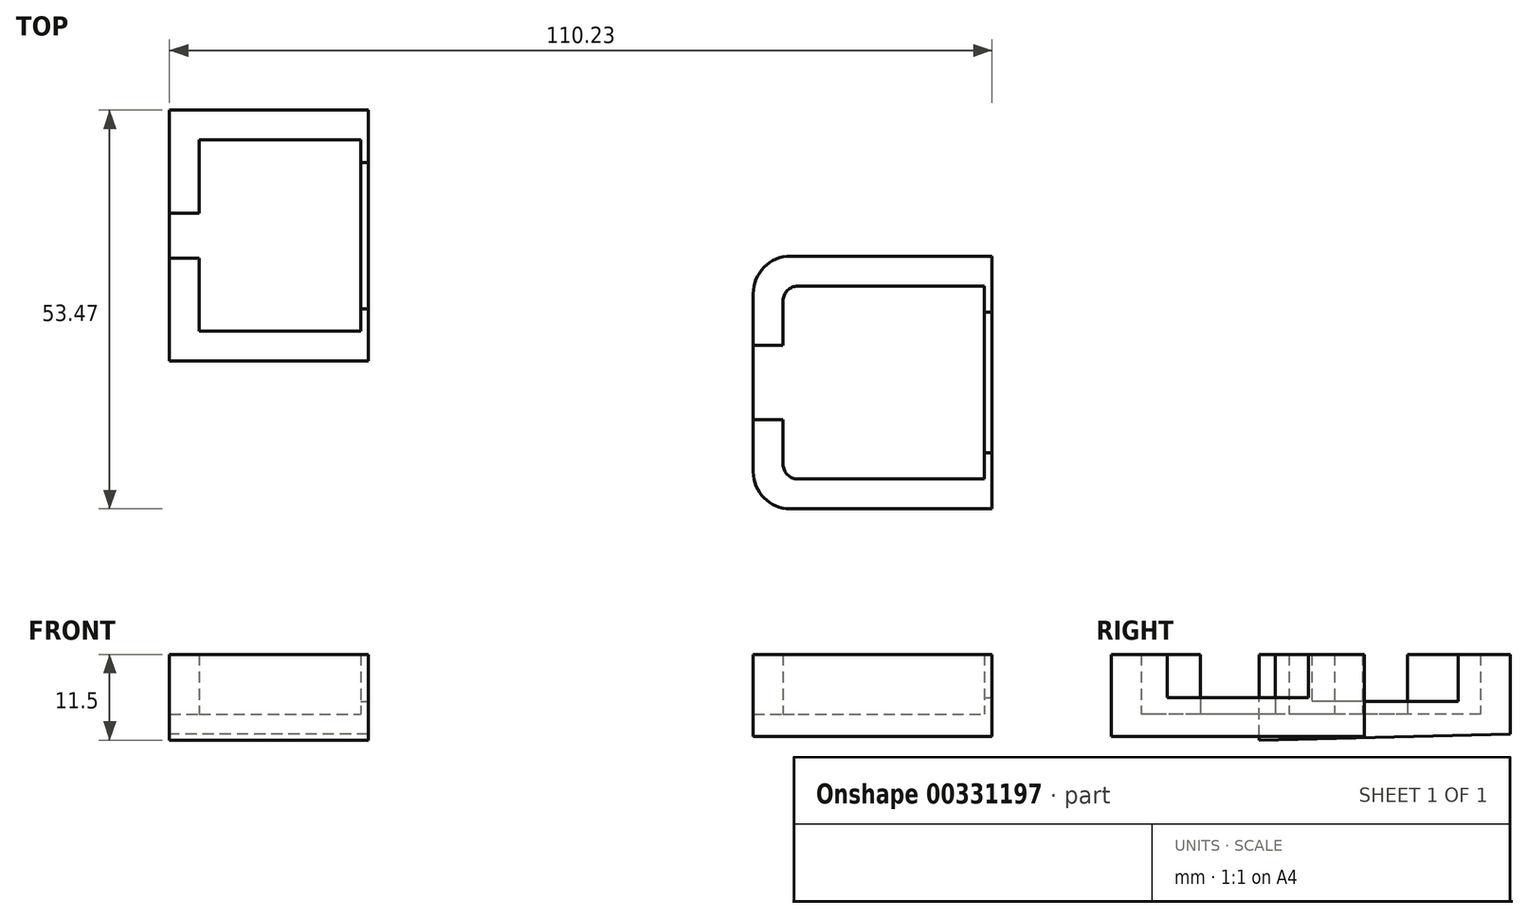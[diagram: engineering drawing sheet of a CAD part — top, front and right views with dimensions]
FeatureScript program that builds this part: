
annotation { "Feature Type Name" : "Feature", "Feature Type Description" : "" }
export const myFeature = defineFeature(function(context is Context, id is Id, definition is map)
    precondition{}
    {
        {
            var Q0;
            Q0=qCreatedBy(makeId("Top.planeOp"),FACE);
            var sketch = newSketch(context, id + "F0", { "sketchPlane" : qUnion([Q0])});
            skLineSegment(sketch, "E0.top", {"start": v(-65.73, 43.8) * mm, "end": v(-61.73, 43.8) * mm});
            skLineSegment(sketch, "E1.top", {"start": v(-65.73, 37.8) * mm, "end": v(-61.73, 37.8) * mm});
            skLineSegment(sketch, "E2.top", {"start": v(-61.73, 27.98) * mm, "end": v(-40.08, 27.98) * mm});
            skLineSegment(sketch, "E2.left", {"start": v(-61.73, 23.98) * mm, "end": v(-61.73, 27.98) * mm});
            skLineSegment(sketch, "E2.right", {"start": v(-40.08, 23.98) * mm, "end": v(-40.08, 27.98) * mm});
            skPoint(sketch, "E3.oppositeSnap0", {"position": v(-61.73, 53.63) * mm});
            skLineSegment(sketch, "E3.top", {"start": v(-61.73, 53.63) * mm, "end": v(-40.08, 53.63) * mm});
            skLineSegment(sketch, "E3.left", {"start": v(-61.73, 57.63) * mm, "end": v(-61.73, 53.63) * mm});
            skLineSegment(sketch, "E3.right", {"start": v(-40.08, 57.63) * mm, "end": v(-40.08, 53.63) * mm});
            skLineSegment(sketch, "E4.top", {"start": v(-40.08, 23.98) * mm, "end": v(-39.08, 23.98) * mm});
            skLineSegment(sketch, "E4.right", {"start": v(-39.08, 57.63) * mm, "end": v(-39.08, 23.98) * mm});
            skLineSegment(sketch, "E5", {"start": v(-40.08, 53.63) * mm, "end": v(-40.08, 27.98) * mm});
            skLineSegment(sketch, "E6", {"start": v(-40.08, 57.63) * mm, "end": v(-39.08, 57.63) * mm});
            skLineSegment(sketch, "E7", {"start": v(-61.73, 53.63) * mm, "end": v(-61.73, 43.8) * mm});
            skLineSegment(sketch, "E8", {"start": v(-65.73, 57.63) * mm, "end": v(-61.73, 57.63) * mm});
            skLineSegment(sketch, "E9", {"start": v(-61.73, 57.63) * mm, "end": v(-40.08, 57.63) * mm});
            skLineSegment(sketch, "E10", {"start": v(-61.73, 37.8) * mm, "end": v(-61.73, 27.98) * mm});
            skLineSegment(sketch, "E11", {"start": v(-65.73, 23.98) * mm, "end": v(-61.73, 23.98) * mm});
            skLineSegment(sketch, "E12", {"start": v(-40.08, 23.98) * mm, "end": v(-61.73, 23.98) * mm});
            skLineSegment(sketch, "E13", {"start": v(-39.08, 23.98) * mm, "end": v(-40.08, 23.98) * mm});
            skLineSegment(sketch, "E14", {"start": v(-65.73, 57.63) * mm, "end": v(-65.73, 43.8) * mm});
            skLineSegment(sketch, "E15", {"start": v(-65.73, 43.8) * mm, "end": v(-65.73, 37.8) * mm});
            skLineSegment(sketch, "E16", {"start": v(-65.73, 37.8) * mm, "end": v(-65.73, 23.98) * mm});
            skPoint(sketch, "E17", {"position": v(-65.73, 40.8) * mm});
            skPoint(sketch, "E18", {"position": v(-40.08, 40.8) * mm});
            skLineSegment(sketch, "E19", {"start": v(-40.08, 50.63) * mm, "end": v(-39.08, 50.63) * mm});
            skLineSegment(sketch, "E20", {"start": v(-40.08, 30.98) * mm, "end": v(-39.08, 30.98) * mm});
            skLineSegment(sketch, "E21.top", {"start": v(12.5, 26.1) * mm, "end": v(16.5, 26.1) * mm});
            skLineSegment(sketch, "E22.top", {"start": v(12.5, 16.1) * mm, "end": v(16.5, 16.1) * mm});
            skLineSegment(sketch, "E23.top", {"start": v(16.5, 8.16) * mm, "end": v(43.5, 8.16) * mm});
            skLineSegment(sketch, "E23.left", {"start": v(16.5, 4.16) * mm, "end": v(16.5, 8.16) * mm});
            skLineSegment(sketch, "E23.right", {"start": v(43.5, 4.16) * mm, "end": v(43.5, 8.16) * mm});
            skPoint(sketch, "E24.oppositeSnap0", {"position": v(16.5, 34.04) * mm});
            skLineSegment(sketch, "E24.top", {"start": v(16.5, 34.04) * mm, "end": v(43.5, 34.04) * mm});
            skLineSegment(sketch, "E24.left", {"start": v(16.5, 38.04) * mm, "end": v(16.5, 34.04) * mm});
            skLineSegment(sketch, "E24.right", {"start": v(43.5, 38.04) * mm, "end": v(43.5, 34.04) * mm});
            skLineSegment(sketch, "E25.top", {"start": v(43.5, 4.16) * mm, "end": v(44.5, 4.16) * mm});
            skLineSegment(sketch, "E25.right", {"start": v(44.5, 38.04) * mm, "end": v(44.5, 4.16) * mm});
            skLineSegment(sketch, "E26", {"start": v(43.5, 34.04) * mm, "end": v(43.5, 8.16) * mm});
            skLineSegment(sketch, "E27", {"start": v(43.5, 38.04) * mm, "end": v(44.5, 38.04) * mm});
            skLineSegment(sketch, "E28", {"start": v(16.5, 34.04) * mm, "end": v(16.5, 26.1) * mm});
            skLineSegment(sketch, "E29", {"start": v(12.5, 38.04) * mm, "end": v(16.5, 38.04) * mm});
            skLineSegment(sketch, "E30", {"start": v(16.5, 38.04) * mm, "end": v(43.5, 38.04) * mm});
            skLineSegment(sketch, "E31", {"start": v(16.5, 16.1) * mm, "end": v(16.5, 8.16) * mm});
            skLineSegment(sketch, "E32", {"start": v(12.5, 4.16) * mm, "end": v(16.5, 4.16) * mm});
            skLineSegment(sketch, "E33", {"start": v(43.5, 4.16) * mm, "end": v(16.5, 4.16) * mm});
            skLineSegment(sketch, "E34", {"start": v(44.5, 4.16) * mm, "end": v(43.5, 4.16) * mm});
            skLineSegment(sketch, "E35", {"start": v(12.5, 38.04) * mm, "end": v(12.5, 26.1) * mm});
            skLineSegment(sketch, "E36", {"start": v(12.5, 26.1) * mm, "end": v(12.5, 16.1) * mm});
            skLineSegment(sketch, "E37", {"start": v(12.5, 16.1) * mm, "end": v(12.5, 4.16) * mm});
            skPoint(sketch, "E38", {"position": v(12.5, 21.1) * mm});
            skPoint(sketch, "E39", {"position": v(43.5, 21.1) * mm});
            skLineSegment(sketch, "E40", {"start": v(43.5, 30.54) * mm, "end": v(44.5, 30.54) * mm});
            skLineSegment(sketch, "E41", {"start": v(43.5, 11.66) * mm, "end": v(44.5, 11.66) * mm});
            skSolve(sketch);
        }
        {
            var Q0;
            Q0=makeQuery(id+"F0.imprint","IMPRINT",FACE,{"disambiguationData":[TD([[makeQuery(id+"F0.imprint","IMPRINT",EDGE,{"derivedFrom":sQuery(id+"F0.wireOp",EDGE,"E0.top")}),1.0]])]});
            var Q1;
            Q1=makeQuery(id+"F0.imprint","IMPRINT",FACE,{"disambiguationData":[TD([[makeQuery(id+"F0.imprint","IMPRINT",EDGE,{"derivedFrom":sQuery(id+"F0.wireOp",EDGE,"E3.top")}),1.0]])]});
            var Q2;
            Q2=makeQuery(id+"F0.imprint","IMPRINT",FACE,{"disambiguationData":[TD([[makeQuery(id+"F0.imprint","IMPRINT",EDGE,{"derivedFrom":sQuery(id+"F0.wireOp",EDGE,"E0.top")}),-1.0]])]});
            var Q3;
            Q3=makeQuery(id+"F0.imprint","IMPRINT",FACE,{"disambiguationData":[TD([[makeQuery(id+"F0.imprint","IMPRINT",EDGE,{"derivedFrom":sQuery(id+"F0.wireOp",EDGE,"E1.top")}),-1.0]])]});
            var Q4;
            Q4=makeQuery(id+"F0.imprint","IMPRINT",FACE,{"disambiguationData":[TD([[makeQuery(id+"F0.imprint","IMPRINT",EDGE,{"derivedFrom":sQuery(id+"F0.wireOp",EDGE,"E2.top")}),-1.0]])]});
            var Q5;
            Q5=makeQuery(id+"F0.imprint","IMPRINT",FACE,{"disambiguationData":[TD([[makeQuery(id+"F0.imprint","IMPRINT",EDGE,{"derivedFrom":sQuery(id+"F0.wireOp",EDGE,"E2.right")}),-1.0]])]});
            var Q6;
            {var subQ0=sQuery(id+"F0.wireOp",EDGE,"E19");Q6=makeQuery(id+"F0.imprint","IMPRINT",FACE,{"disambiguationData":[TD([[makeQuery(id+"F0.imprint","IMPRINT",EDGE,{"derivedFrom":subQ0}),-1.0]])]});}
            var Q7;
            {var subQ3=sQuery(id+"F0.wireOp",EDGE,"E3.right");Q7=makeQuery(id+"F0.imprint","IMPRINT",FACE,{"disambiguationData":[TD([[makeQuery(id+"F0.imprint","IMPRINT",EDGE,{"derivedFrom":subQ3}),1.0]])]});}
            extrude(context, id + "F1", {"entities" : qUnion([Q0, Q1, Q2, Q3, Q4, Q5, Q6, Q7]), "oppositeDirection" : true, "depth" : 6 * mm});
        }
        {
            var Q0;
            Q0=makeQuery(id+"F0.imprint","IMPRINT",FACE,{"disambiguationData":[TD([[makeQuery(id+"F0.imprint","IMPRINT",EDGE,{"derivedFrom":sQuery(id+"F0.wireOp",EDGE,"E0.top")}),1.0]])]});
            var Q1;
            Q1=makeQuery(id+"F0.imprint","IMPRINT",FACE,{"disambiguationData":[TD([[makeQuery(id+"F0.imprint","IMPRINT",EDGE,{"derivedFrom":sQuery(id+"F0.wireOp",EDGE,"E3.top")}),1.0]])]});
            var Q2;
            Q2=makeQuery(id+"F0.imprint","IMPRINT",FACE,{"disambiguationData":[TD([[makeQuery(id+"F0.imprint","IMPRINT",EDGE,{"derivedFrom":sQuery(id+"F0.wireOp",EDGE,"E1.top")}),-1.0]])]});
            var Q3;
            Q3=makeQuery(id+"F0.imprint","IMPRINT",FACE,{"disambiguationData":[TD([[makeQuery(id+"F0.imprint","IMPRINT",EDGE,{"derivedFrom":sQuery(id+"F0.wireOp",EDGE,"E2.top")}),-1.0]])]});
            var Q4;
            {var subQ4=sQuery(id+"F0.wireOp",EDGE,"E2.right");Q4=makeQuery(id+"F0.imprint","IMPRINT",FACE,{"disambiguationData":[TD([[makeQuery(id+"F0.imprint","IMPRINT",EDGE,{"derivedFrom":subQ4}),-1.0]])]});}
            var Q5;
            {var subQ3=sQuery(id+"F0.wireOp",EDGE,"E3.right");Q5=makeQuery(id+"F0.imprint","IMPRINT",FACE,{"disambiguationData":[TD([[makeQuery(id+"F0.imprint","IMPRINT",EDGE,{"derivedFrom":subQ3}),1.0]])]});}
            extrude(context, id + "F2", {"entities" : qUnion([Q0, Q1, Q2, Q3, Q4, Q5]), "operationType" : NewBodyOperationType.ADD, "depth" : 8 * mm});
        }
        {
            var Q0;
            {var subQ0=sQuery(id+"F0.wireOp",EDGE,"E19");Q0=makeQuery(id+"F0.imprint","IMPRINT",FACE,{"disambiguationData":[TD([[makeQuery(id+"F0.imprint","IMPRINT",EDGE,{"derivedFrom":subQ0}),-1.0]])]});}
            extrude(context, id + "F3", {"entities" : qUnion([Q0]), "operationType" : NewBodyOperationType.ADD, "depth" : 1.7 * mm});
        }
        {
            var Q0;
            {var subQ0=sQuery(id+"F0.wireOp",EDGE,"E16");var subQ1=sQuery(id+"F0.wireOp",EDGE,"E14");Q0=makeQuery(id+"F2.boolean.opBoolean","MERGE",FACE,{"derivedFrom":[makeQuery(id+"F1.opExtrude","SWEPT_FACE",FACE,{"disambiguationData":[OSD([subQ1,sQuery(id+"F0.wireOp",EDGE,"E15"),subQ0])]}),makeQuery(id+"F2.opExtrude","SWEPT_FACE",FACE,{"disambiguationData":[OSD([subQ1])]}),makeQuery(id+"F2.opExtrude","SWEPT_FACE",FACE,{"disambiguationData":[OSD([subQ0])]})]});}
            var sketch = newSketch(context, id + "F4", { "sketchPlane" : qUnion([Q0])});
            skLineSegment(sketch, "E42", {"start": v(-57.63, -2.7) * mm, "end": v(-23.98, -3.5) * mm});
            skSolve(sketch);
        }
        {
            var Q0;
            {var subQ0=sQuery(id+"F4.wireOp",EDGE,"E42");Q0=makeQuery(id+"F4.imprint","IMPRINT",FACE,{"disambiguationData":[TD([[makeQuery(id+"F4.imprint","IMPRINT",EDGE,{"derivedFrom":subQ0}),-1.0]])]});}
            extrude(context, id + "F5", {"entities" : qUnion([Q0]), "operationType" : NewBodyOperationType.REMOVE, "endBound" : BoundingType.UP_TO_NEXT, "oppositeDirection" : true, "depth" : 25 * mm});
        }
        {
            var Q0;
            Q0=makeQuery(id+"F0.imprint","IMPRINT",FACE,{"disambiguationData":[TD([[makeQuery(id+"F0.imprint","IMPRINT",EDGE,{"derivedFrom":sQuery(id+"F0.wireOp",EDGE,"E21.top")}),1.0]])]});
            var Q1;
            Q1=makeQuery(id+"F0.imprint","IMPRINT",FACE,{"disambiguationData":[TD([[makeQuery(id+"F0.imprint","IMPRINT",EDGE,{"derivedFrom":sQuery(id+"F0.wireOp",EDGE,"E24.top")}),1.0]])]});
            var Q2;
            {var subQ3=sQuery(id+"F0.wireOp",EDGE,"E24.right");Q2=makeQuery(id+"F0.imprint","IMPRINT",FACE,{"disambiguationData":[TD([[makeQuery(id+"F0.imprint","IMPRINT",EDGE,{"derivedFrom":subQ3}),1.0]])]});}
            var Q3;
            {var subQ0=sQuery(id+"F0.wireOp",EDGE,"E40");Q3=makeQuery(id+"F0.imprint","IMPRINT",FACE,{"disambiguationData":[TD([[makeQuery(id+"F0.imprint","IMPRINT",EDGE,{"derivedFrom":subQ0}),-1.0]])]});}
            var Q4;
            {var subQ4=sQuery(id+"F0.wireOp",EDGE,"E23.right");Q4=makeQuery(id+"F0.imprint","IMPRINT",FACE,{"disambiguationData":[TD([[makeQuery(id+"F0.imprint","IMPRINT",EDGE,{"derivedFrom":subQ4}),-1.0]])]});}
            var Q5;
            Q5=makeQuery(id+"F0.imprint","IMPRINT",FACE,{"disambiguationData":[TD([[makeQuery(id+"F0.imprint","IMPRINT",EDGE,{"derivedFrom":sQuery(id+"F0.wireOp",EDGE,"E23.top")}),-1.0]])]});
            var Q6;
            Q6=makeQuery(id+"F0.imprint","IMPRINT",FACE,{"disambiguationData":[TD([[makeQuery(id+"F0.imprint","IMPRINT",EDGE,{"derivedFrom":sQuery(id+"F0.wireOp",EDGE,"E22.top")}),-1.0]])]});
            var Q7;
            Q7=makeQuery(id+"F0.imprint","IMPRINT",FACE,{"disambiguationData":[TD([[makeQuery(id+"F0.imprint","IMPRINT",EDGE,{"derivedFrom":sQuery(id+"F0.wireOp",EDGE,"E21.top")}),-1.0]])]});
            extrude(context, id + "F6", {"entities" : qUnion([Q0, Q1, Q2, Q3, Q4, Q5, Q6, Q7]), "oppositeDirection" : true, "depth" : 3 * mm});
        }
        {
            var Q0;
            Q0=makeQuery(id+"F0.imprint","IMPRINT",FACE,{"disambiguationData":[TD([[makeQuery(id+"F0.imprint","IMPRINT",EDGE,{"derivedFrom":sQuery(id+"F0.wireOp",EDGE,"E21.top")}),1.0]])]});
            var Q1;
            Q1=makeQuery(id+"F0.imprint","IMPRINT",FACE,{"disambiguationData":[TD([[makeQuery(id+"F0.imprint","IMPRINT",EDGE,{"derivedFrom":sQuery(id+"F0.wireOp",EDGE,"E24.top")}),1.0]])]});
            var Q2;
            Q2=makeQuery(id+"F0.imprint","IMPRINT",FACE,{"disambiguationData":[TD([[makeQuery(id+"F0.imprint","IMPRINT",EDGE,{"derivedFrom":sQuery(id+"F0.wireOp",EDGE,"E22.top")}),-1.0]])]});
            var Q3;
            Q3=makeQuery(id+"F0.imprint","IMPRINT",FACE,{"disambiguationData":[TD([[makeQuery(id+"F0.imprint","IMPRINT",EDGE,{"derivedFrom":sQuery(id+"F0.wireOp",EDGE,"E23.top")}),-1.0]])]});
            var Q4;
            {var subQ4=sQuery(id+"F0.wireOp",EDGE,"E23.right");Q4=makeQuery(id+"F0.imprint","IMPRINT",FACE,{"disambiguationData":[TD([[makeQuery(id+"F0.imprint","IMPRINT",EDGE,{"derivedFrom":subQ4}),-1.0]])]});}
            var Q5;
            {var subQ3=sQuery(id+"F0.wireOp",EDGE,"E24.right");Q5=makeQuery(id+"F0.imprint","IMPRINT",FACE,{"disambiguationData":[TD([[makeQuery(id+"F0.imprint","IMPRINT",EDGE,{"derivedFrom":subQ3}),1.0]])]});}
            extrude(context, id + "F7", {"entities" : qUnion([Q0, Q1, Q2, Q3, Q4, Q5]), "operationType" : NewBodyOperationType.ADD, "depth" : 8 * mm});
        }
        {
            var Q0;
            {var subQ0=sQuery(id+"F0.wireOp",EDGE,"E40");Q0=makeQuery(id+"F0.imprint","IMPRINT",FACE,{"disambiguationData":[TD([[makeQuery(id+"F0.imprint","IMPRINT",EDGE,{"derivedFrom":subQ0}),-1.0]])]});}
            extrude(context, id + "F8", {"entities" : qUnion([Q0]), "operationType" : NewBodyOperationType.ADD, "depth" : 2.2 * mm});
        }
        {
            var Q0;
            Q0=makeQuery(id+"F7.opExtrude","SWEPT_EDGE",EDGE,{"disambiguationData":[OSD([sQuery(id+"F0.wireOp",EDGE,"E24.top"),sQuery(id+"F0.wireOp",EDGE,"E24.left"),sQuery(id+"F0.wireOp",EDGE,"E28")])]});
            var Q1;
            Q1=makeQuery(id+"F7.opExtrude","SWEPT_EDGE",EDGE,{"disambiguationData":[OSD([sQuery(id+"F0.wireOp",EDGE,"E23.top"),sQuery(id+"F0.wireOp",EDGE,"E23.left"),sQuery(id+"F0.wireOp",EDGE,"E31")])]});
            fillet(context, id + "F9", {"entities" : qUnion([Q0, Q1]), "radius" : 2 * mm, "tangentPropagation" : true, "allowEdgeOverflow" : false});
        }
        {
            var Q0;
            {var subQ0=sQuery(id+"F0.wireOp",EDGE,"E35");var subQ1=sQuery(id+"F0.wireOp",EDGE,"E29");Q0=makeQuery(id+"F7.boolean.opBoolean","MERGE",EDGE,{"derivedFrom":[makeQuery(id+"F6.opExtrude","SWEPT_EDGE",EDGE,{"disambiguationData":[OSD([subQ1,subQ0])]}),makeQuery(id+"F7.opExtrude","SWEPT_EDGE",EDGE,{"disambiguationData":[OSD([subQ1,subQ0])]})]});}
            var Q1;
            {var subQ0=sQuery(id+"F0.wireOp",EDGE,"E37");var subQ1=sQuery(id+"F0.wireOp",EDGE,"E32");Q1=makeQuery(id+"F7.boolean.opBoolean","MERGE",EDGE,{"derivedFrom":[makeQuery(id+"F6.opExtrude","SWEPT_EDGE",EDGE,{"disambiguationData":[OSD([subQ1,subQ0])]}),makeQuery(id+"F7.opExtrude","SWEPT_EDGE",EDGE,{"disambiguationData":[OSD([subQ1,subQ0])]})]});}
            fillet(context, id + "F10", {"entities" : qUnion([Q0, Q1]), "radius" : 5 * mm, "tangentPropagation" : true, "allowEdgeOverflow" : false});
        }
    });
